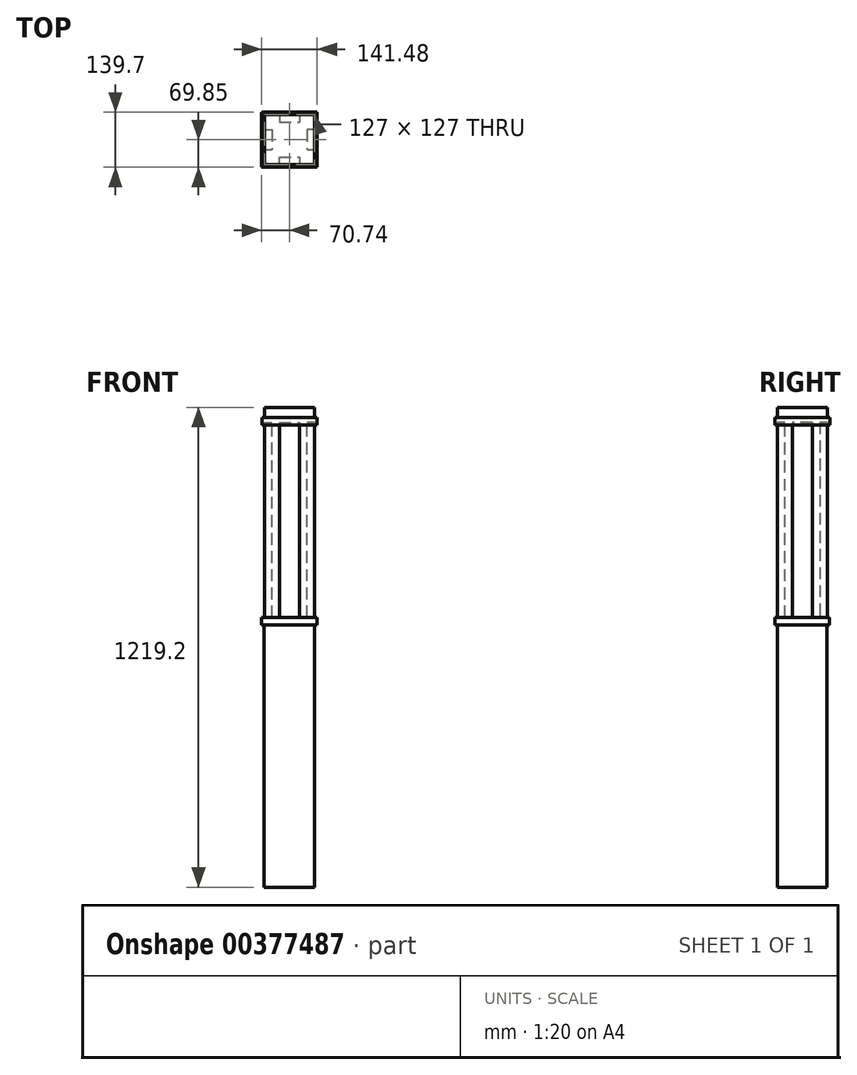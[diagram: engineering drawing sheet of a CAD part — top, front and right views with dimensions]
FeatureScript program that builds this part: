
annotation { "Feature Type Name" : "Feature", "Feature Type Description" : "" }
export const myFeature = defineFeature(function(context is Context, id is Id, definition is map)
    precondition{}
    {
        {
            var Q0;
            Q0=qCreatedBy(makeId("Top.planeOp"),FACE);
            var sketch = newSketch(context, id + "F0", { "sketchPlane" : qUnion([Q0])});
            skLineSegment(sketch, "E0.bottom", {"start": v(-64.39, 62.74) * mm, "end": v(64.39, 62.74) * mm});
            skLineSegment(sketch, "E0.top", {"start": v(-64.39, -62.74) * mm, "end": v(64.39, -62.74) * mm});
            skLineSegment(sketch, "E0.left", {"start": v(-64.39, 62.74) * mm, "end": v(-64.39, -62.74) * mm});
            skLineSegment(sketch, "E0.right", {"start": v(64.39, 62.74) * mm, "end": v(64.39, -62.74) * mm});
            skPoint(sketch, "E0.middle", {"position": v(0, 0) * mm});
            skSolve(sketch);
        }
        {
            var Q0;
            Q0=qSketchRegion(id+"F0",true);
            extrude(context, id + "F1", {"entities" : qUnion([Q0]), "depth" : 673.1 * mm, "offsetDistance" : 25.4 * mm});
        }
        {
            var Q0;
            Q0=makeQuery(id+"F1.opExtrude","CAP_FACE",FACE,{"disambiguationData":[OSD([sQuery(id+"F0.wireOp",EDGE,"E0.bottom"),sQuery(id+"F0.wireOp",EDGE,"E0.top"),sQuery(id+"F0.wireOp",EDGE,"E0.left"),sQuery(id+"F0.wireOp",EDGE,"E0.right")])],"isStart":false});
            var sketch = newSketch(context, id + "F2", { "sketchPlane" : qUnion([Q0])});
            skLineSegment(sketch, "E1.bottom", {"start": v(-44.45, 44.45) * mm, "end": v(44.45, 44.45) * mm});
            skLineSegment(sketch, "E1.top", {"start": v(-44.45, -44.45) * mm, "end": v(44.45, -44.45) * mm});
            skLineSegment(sketch, "E1.left", {"start": v(-44.45, 44.45) * mm, "end": v(-44.45, -44.45) * mm});
            skLineSegment(sketch, "E1.right", {"start": v(44.45, 44.45) * mm, "end": v(44.45, -44.45) * mm});
            skPoint(sketch, "E1.middle", {"position": v(0, 0) * mm});
            skSolve(sketch);
        }
        {
            var Q0;
            Q0=qSketchRegion(id+"F2",true);
            extrude(context, id + "F3", {"entities" : qUnion([Q0]), "operationType" : NewBodyOperationType.ADD, "depth" : 508 * mm, "offsetDistance" : 25.4 * mm});
        }
        {
            var Q0;
            Q0=makeQuery(id+"F1.opExtrude","CAP_FACE",FACE,{"disambiguationData":[OSD([sQuery(id+"F0.wireOp",EDGE,"E0.bottom"),sQuery(id+"F0.wireOp",EDGE,"E0.top"),sQuery(id+"F0.wireOp",EDGE,"E0.left"),sQuery(id+"F0.wireOp",EDGE,"E0.right")])],"isStart":false});
            var sketch = newSketch(context, id + "F4", { "sketchPlane" : qUnion([Q0])});
            skLineSegment(sketch, "E2.bottom", {"start": v(-44.45, 44.45) * mm, "end": v(44.45, 44.45) * mm});
            skLineSegment(sketch, "E2.top", {"start": v(-44.45, -44.45) * mm, "end": v(44.45, -44.45) * mm});
            skLineSegment(sketch, "E2.left", {"start": v(-44.45, 44.45) * mm, "end": v(-44.45, -44.45) * mm});
            skLineSegment(sketch, "E2.right", {"start": v(44.45, 44.45) * mm, "end": v(44.45, -44.45) * mm});
            skPoint(sketch, "E2.middle", {"position": v(0, 0) * mm});
            skLineSegment(sketch, "E3.0", {"start": v(-70.74, 69.09) * mm, "end": v(70.74, 69.09) * mm});
            skLineSegment(sketch, "E3.1", {"start": v(-70.74, 69.09) * mm, "end": v(-70.74, -69.09) * mm});
            skLineSegment(sketch, "E3.2", {"start": v(-70.74, -69.09) * mm, "end": v(70.74, -69.09) * mm});
            skLineSegment(sketch, "E3.3", {"start": v(70.74, 69.09) * mm, "end": v(70.74, -69.09) * mm});
            skSolve(sketch);
        }
        {
            var Q0;
            Q0=qSketchRegion(id+"F4",true);
            extrude(context, id + "F5", {"entities" : qUnion([Q0]), "operationType" : NewBodyOperationType.ADD, "depth" : 12.7 * mm, "offsetDistance" : 25.4 * mm});
        }
        {
            var Q0;
            Q0=makeQuery(id+"F5.opExtrude","CAP_FACE",FACE,{"disambiguationData":[OSD([sQuery(id+"F4.wireOp",EDGE,"E2.bottom"),sQuery(id+"F4.wireOp",EDGE,"E2.top"),sQuery(id+"F4.wireOp",EDGE,"E2.left"),sQuery(id+"F4.wireOp",EDGE,"E2.right"),sQuery(id+"F4.wireOp",EDGE,"E3.0"),sQuery(id+"F4.wireOp",EDGE,"E3.1"),sQuery(id+"F4.wireOp",EDGE,"E3.2"),sQuery(id+"F4.wireOp",EDGE,"E3.3")])],"isStart":true});
            var sketch = newSketch(context, id + "F6", { "sketchPlane" : qUnion([Q0])});
            skLineSegment(sketch, "E4.bottom", {"start": v(-64.39, 62.74) * mm, "end": v(64.39, 62.74) * mm});
            skLineSegment(sketch, "E4.top", {"start": v(-64.39, -62.74) * mm, "end": v(64.39, -62.74) * mm});
            skLineSegment(sketch, "E4.left", {"start": v(-64.39, 62.74) * mm, "end": v(-64.39, -62.74) * mm});
            skLineSegment(sketch, "E4.right", {"start": v(64.39, 62.74) * mm, "end": v(64.39, -62.74) * mm});
            skPoint(sketch, "E4.middle", {"position": v(0, 0) * mm});
            skLineSegment(sketch, "E5.bottom", {"start": v(-70.74, 69.09) * mm, "end": v(70.74, 69.09) * mm});
            skLineSegment(sketch, "E5.top", {"start": v(-70.74, -69.09) * mm, "end": v(70.74, -69.09) * mm});
            skLineSegment(sketch, "E5.left", {"start": v(-70.74, 69.09) * mm, "end": v(-70.74, -69.09) * mm});
            skLineSegment(sketch, "E5.right", {"start": v(70.74, 69.09) * mm, "end": v(70.74, -69.09) * mm});
            skSolve(sketch);
        }
        {
            var Q0;
            Q0=qSketchRegion(id+"F6",true);
            extrude(context, id + "F7", {"entities" : qUnion([Q0]), "operationType" : NewBodyOperationType.ADD, "depth" : 6.35 * mm, "offsetDistance" : 25.4 * mm});
        }
        {
            var Q0;
            Q0=makeQuery(id+"F5.opExtrude","CAP_FACE",FACE,{"disambiguationData":[OSD([sQuery(id+"F4.wireOp",EDGE,"E2.bottom"),sQuery(id+"F4.wireOp",EDGE,"E2.top"),sQuery(id+"F4.wireOp",EDGE,"E2.left"),sQuery(id+"F4.wireOp",EDGE,"E2.right"),sQuery(id+"F4.wireOp",EDGE,"E3.0"),sQuery(id+"F4.wireOp",EDGE,"E3.1"),sQuery(id+"F4.wireOp",EDGE,"E3.2"),sQuery(id+"F4.wireOp",EDGE,"E3.3")])],"isStart":false});
            var sketch = newSketch(context, id + "F8", { "sketchPlane" : qUnion([Q0])});
            skLineSegment(sketch, "E6.bottom", {"start": v(63.5, 63.5) * mm, "end": v(25.4, 63.5) * mm});
            skLineSegment(sketch, "E6.top", {"start": v(63.5, 25.4) * mm, "end": v(25.4, 25.4) * mm});
            skLineSegment(sketch, "E6.left", {"start": v(63.5, 63.5) * mm, "end": v(63.5, 25.4) * mm});
            skLineSegment(sketch, "E6.right", {"start": v(25.4, 63.5) * mm, "end": v(25.4, 25.4) * mm});
            skPoint(sketch, "E6.middle", {"position": v(44.45, 44.45) * mm});
            skLineSegment(sketch, "E7.bottom", {"start": v(25.4, -25.4) * mm, "end": v(63.5, -25.4) * mm});
            skLineSegment(sketch, "E7.top", {"start": v(25.4, -63.5) * mm, "end": v(63.5, -63.5) * mm});
            skLineSegment(sketch, "E7.left", {"start": v(25.4, -25.4) * mm, "end": v(25.4, -63.5) * mm});
            skLineSegment(sketch, "E7.right", {"start": v(63.5, -25.4) * mm, "end": v(63.5, -63.5) * mm});
            skPoint(sketch, "E7.middle", {"position": v(44.45, -44.45) * mm});
            skLineSegment(sketch, "E8.bottom", {"start": v(-63.5, -63.5) * mm, "end": v(-25.4, -63.5) * mm});
            skLineSegment(sketch, "E8.top", {"start": v(-63.5, -25.4) * mm, "end": v(-25.4, -25.4) * mm});
            skLineSegment(sketch, "E8.left", {"start": v(-63.5, -63.5) * mm, "end": v(-63.5, -25.4) * mm});
            skLineSegment(sketch, "E8.right", {"start": v(-25.4, -63.5) * mm, "end": v(-25.4, -25.4) * mm});
            skPoint(sketch, "E8.middle", {"position": v(-44.45, -44.45) * mm});
            skLineSegment(sketch, "E9.bottom", {"start": v(-63.5, 63.5) * mm, "end": v(-25.4, 63.5) * mm});
            skLineSegment(sketch, "E9.top", {"start": v(-63.5, 25.4) * mm, "end": v(-25.4, 25.4) * mm});
            skLineSegment(sketch, "E9.left", {"start": v(-63.5, 63.5) * mm, "end": v(-63.5, 25.4) * mm});
            skLineSegment(sketch, "E9.right", {"start": v(-25.4, 63.5) * mm, "end": v(-25.4, 25.4) * mm});
            skPoint(sketch, "E9.middle", {"position": v(-44.45, 44.45) * mm});
            skSolve(sketch);
        }
        {
            var Q0;
            Q0=qSketchRegion(id+"F8",true);
            extrude(context, id + "F9", {"entities" : qUnion([Q0]), "operationType" : NewBodyOperationType.ADD, "depth" : 495.3 * mm, "offsetDistance" : 25.4 * mm});
        }
        {
            var Q0;
            Q0=makeQuery(id+"F9.boolean.opBoolean","MERGE",FACE,{"derivedFrom":[makeQuery(id+"F3.opExtrude","CAP_FACE",FACE,{"disambiguationData":[OSD([sQuery(id+"F2.wireOp",EDGE,"E1.bottom"),sQuery(id+"F2.wireOp",EDGE,"E1.top"),sQuery(id+"F2.wireOp",EDGE,"E1.left"),sQuery(id+"F2.wireOp",EDGE,"E1.right")])],"isStart":false}),makeQuery(id+"F9.opExtrude","CAP_FACE",FACE,{"disambiguationData":[OSD([sQuery(id+"F8.wireOp",EDGE,"E6.bottom"),sQuery(id+"F8.wireOp",EDGE,"E6.top"),sQuery(id+"F8.wireOp",EDGE,"E6.left"),sQuery(id+"F8.wireOp",EDGE,"E6.right")])],"isStart":false}),makeQuery(id+"F9.opExtrude","CAP_FACE",FACE,{"disambiguationData":[OSD([sQuery(id+"F8.wireOp",EDGE,"E7.bottom"),sQuery(id+"F8.wireOp",EDGE,"E7.top"),sQuery(id+"F8.wireOp",EDGE,"E7.left"),sQuery(id+"F8.wireOp",EDGE,"E7.right")])],"isStart":false}),makeQuery(id+"F9.opExtrude","CAP_FACE",FACE,{"disambiguationData":[OSD([sQuery(id+"F8.wireOp",EDGE,"E8.bottom"),sQuery(id+"F8.wireOp",EDGE,"E8.top"),sQuery(id+"F8.wireOp",EDGE,"E8.left"),sQuery(id+"F8.wireOp",EDGE,"E8.right")])],"isStart":false}),makeQuery(id+"F9.opExtrude","CAP_FACE",FACE,{"disambiguationData":[OSD([sQuery(id+"F8.wireOp",EDGE,"E9.bottom"),sQuery(id+"F8.wireOp",EDGE,"E9.top"),sQuery(id+"F8.wireOp",EDGE,"E9.left"),sQuery(id+"F8.wireOp",EDGE,"E9.right")])],"isStart":false})]});
            var sketch = newSketch(context, id + "F10", { "sketchPlane" : qUnion([Q0])});
            skLineSegment(sketch, "E10.bottom", {"start": v(-63.5, -63.5) * mm, "end": v(63.5, -63.5) * mm});
            skLineSegment(sketch, "E10.top", {"start": v(-63.5, 63.5) * mm, "end": v(63.5, 63.5) * mm});
            skLineSegment(sketch, "E10.left", {"start": v(-63.5, -63.5) * mm, "end": v(-63.5, 63.5) * mm});
            skLineSegment(sketch, "E10.right", {"start": v(63.5, -63.5) * mm, "end": v(63.5, 63.5) * mm});
            skPoint(sketch, "E10.middle", {"position": v(0, 0) * mm});
            skLineSegment(sketch, "E11.0", {"start": v(-69.85, 69.85) * mm, "end": v(69.85, 69.85) * mm});
            skLineSegment(sketch, "E11.1", {"start": v(-69.85, -69.85) * mm, "end": v(-69.85, 69.85) * mm});
            skLineSegment(sketch, "E11.2", {"start": v(-69.85, -69.85) * mm, "end": v(69.85, -69.85) * mm});
            skLineSegment(sketch, "E11.3", {"start": v(69.85, -69.85) * mm, "end": v(69.85, 69.85) * mm});
            skSolve(sketch);
        }
        {
            var Q0;
            Q0=qSketchRegion(id+"F10",true);
            extrude(context, id + "F11", {"entities" : qUnion([Q0]), "operationType" : NewBodyOperationType.ADD, "oppositeDirection" : true, "depth" : 6.35 * mm, "offsetDistance" : 25.4 * mm});
        }
        {
            var Q0;
            Q0=makeQuery(id+"F11.boolean.opBoolean","MERGE",FACE,{"derivedFrom":[makeQuery(id+"F9.boolean.opBoolean","MERGE",FACE,{"derivedFrom":[makeQuery(id+"F3.opExtrude","CAP_FACE",FACE,{"disambiguationData":[OSD([sQuery(id+"F2.wireOp",EDGE,"E1.bottom"),sQuery(id+"F2.wireOp",EDGE,"E1.top"),sQuery(id+"F2.wireOp",EDGE,"E1.left"),sQuery(id+"F2.wireOp",EDGE,"E1.right")])],"isStart":false}),makeQuery(id+"F9.opExtrude","CAP_FACE",FACE,{"disambiguationData":[OSD([sQuery(id+"F8.wireOp",EDGE,"E6.bottom"),sQuery(id+"F8.wireOp",EDGE,"E6.top"),sQuery(id+"F8.wireOp",EDGE,"E6.left"),sQuery(id+"F8.wireOp",EDGE,"E6.right")])],"isStart":false}),makeQuery(id+"F9.opExtrude","CAP_FACE",FACE,{"disambiguationData":[OSD([sQuery(id+"F8.wireOp",EDGE,"E7.bottom"),sQuery(id+"F8.wireOp",EDGE,"E7.top"),sQuery(id+"F8.wireOp",EDGE,"E7.left"),sQuery(id+"F8.wireOp",EDGE,"E7.right")])],"isStart":false}),makeQuery(id+"F9.opExtrude","CAP_FACE",FACE,{"disambiguationData":[OSD([sQuery(id+"F8.wireOp",EDGE,"E8.bottom"),sQuery(id+"F8.wireOp",EDGE,"E8.top"),sQuery(id+"F8.wireOp",EDGE,"E8.left"),sQuery(id+"F8.wireOp",EDGE,"E8.right")])],"isStart":false}),makeQuery(id+"F9.opExtrude","CAP_FACE",FACE,{"disambiguationData":[OSD([sQuery(id+"F8.wireOp",EDGE,"E9.bottom"),sQuery(id+"F8.wireOp",EDGE,"E9.top"),sQuery(id+"F8.wireOp",EDGE,"E9.left"),sQuery(id+"F8.wireOp",EDGE,"E9.right")])],"isStart":false})]}),makeQuery(id+"F11.opExtrude","CAP_FACE",FACE,{"disambiguationData":[OSD([sQuery(id+"F10.wireOp",EDGE,"E10.bottom"),sQuery(id+"F10.wireOp",EDGE,"E10.top"),sQuery(id+"F10.wireOp",EDGE,"E10.left"),sQuery(id+"F10.wireOp",EDGE,"E10.right"),sQuery(id+"F10.wireOp",EDGE,"E11.0"),sQuery(id+"F10.wireOp",EDGE,"E11.1"),sQuery(id+"F10.wireOp",EDGE,"E11.2"),sQuery(id+"F10.wireOp",EDGE,"E11.3")])],"isStart":true})]});
            var sketch = newSketch(context, id + "F12", { "sketchPlane" : qUnion([Q0])});
            skLineSegment(sketch, "E12.bottom", {"start": v(-69.85, 69.85) * mm, "end": v(69.85, 69.85) * mm});
            skLineSegment(sketch, "E12.top", {"start": v(-69.85, -69.85) * mm, "end": v(69.85, -69.85) * mm});
            skLineSegment(sketch, "E12.left", {"start": v(-69.85, 69.85) * mm, "end": v(-69.85, -69.85) * mm});
            skLineSegment(sketch, "E12.right", {"start": v(69.85, 69.85) * mm, "end": v(69.85, -69.85) * mm});
            skPoint(sketch, "E12.middle", {"position": v(0, 0) * mm});
            skSolve(sketch);
        }
        {
            var Q0;
            Q0=qSketchRegion(id+"F12",true);
            extrude(context, id + "F13", {"entities" : qUnion([Q0]), "operationType" : NewBodyOperationType.ADD, "depth" : 12.7 * mm, "offsetDistance" : 25.4 * mm});
        }
        {
            var Q0;
            Q0=makeQuery(id+"F13.opExtrude","CAP_FACE",FACE,{"disambiguationData":[OSD([sQuery(id+"F12.wireOp",EDGE,"E12.bottom"),sQuery(id+"F12.wireOp",EDGE,"E12.top"),sQuery(id+"F12.wireOp",EDGE,"E12.left"),sQuery(id+"F12.wireOp",EDGE,"E12.right")])],"isStart":false});
            var sketch = newSketch(context, id + "F14", { "sketchPlane" : qUnion([Q0])});
            skLineSegment(sketch, "E13.0", {"start": v(-63.5, 63.5) * mm, "end": v(63.5, 63.5) * mm});
            skLineSegment(sketch, "E13.1", {"start": v(-63.5, -63.5) * mm, "end": v(-63.5, 63.5) * mm});
            skLineSegment(sketch, "E13.2", {"start": v(-63.5, -63.5) * mm, "end": v(63.5, -63.5) * mm});
            skLineSegment(sketch, "E13.3", {"start": v(63.5, -63.5) * mm, "end": v(63.5, 63.5) * mm});
            skSolve(sketch);
        }
        {
            var Q0;
            Q0 = qSketchRegion(id + "F14", true);
            extrude(context, id + "F15", {"entities" : qUnion([Q0]), "operationType" : NewBodyOperationType.ADD, "depth" : 25.4 * mm, "offsetDistance" : 25.4 * mm});
        }
    });
